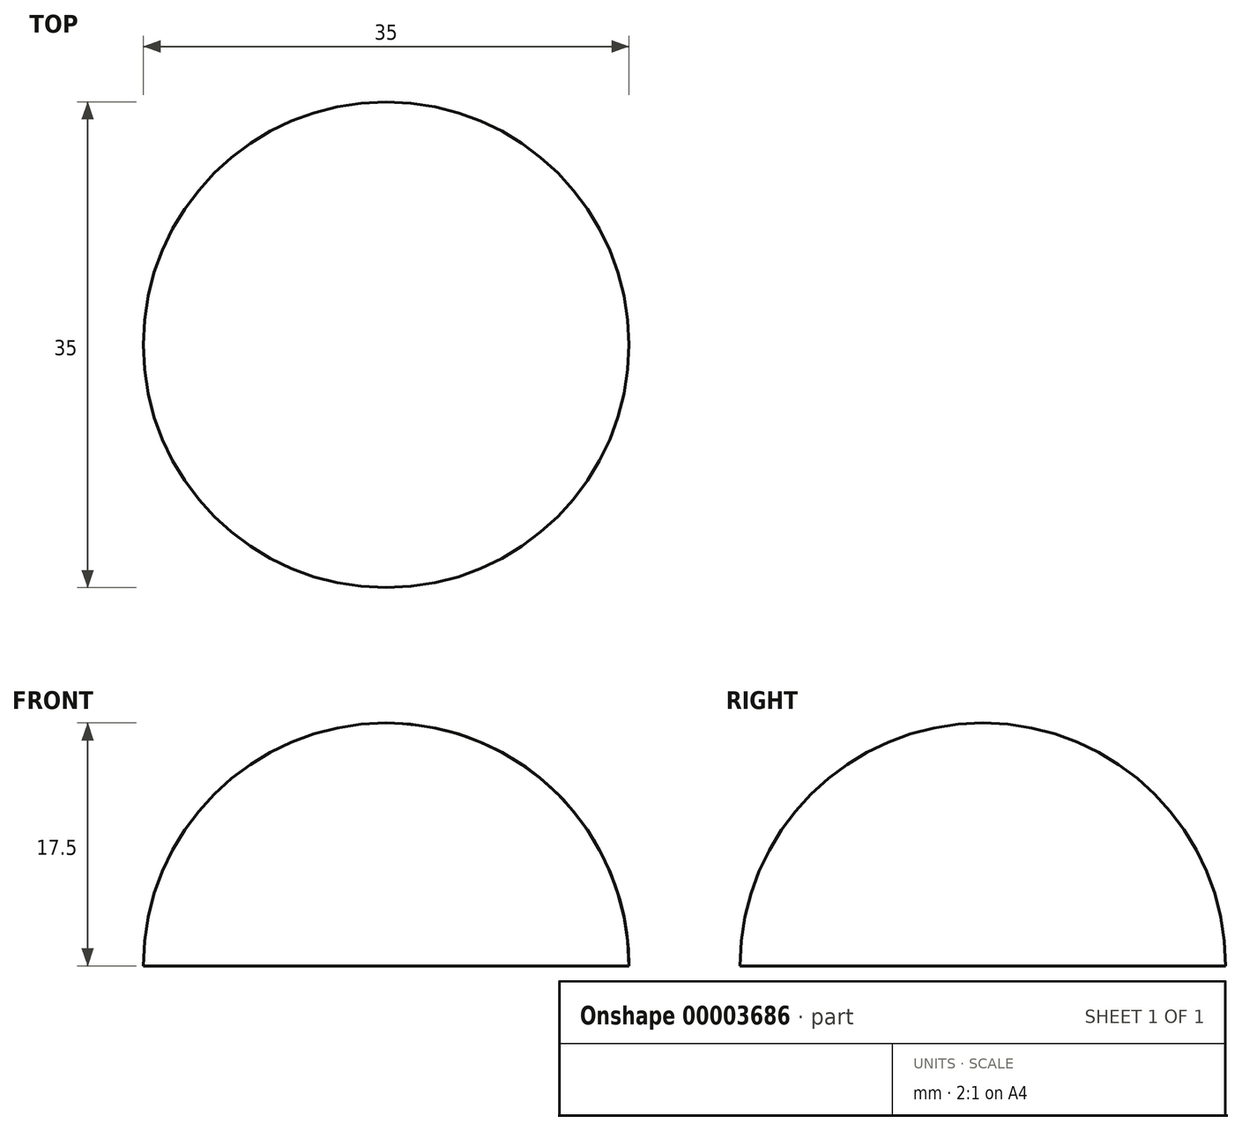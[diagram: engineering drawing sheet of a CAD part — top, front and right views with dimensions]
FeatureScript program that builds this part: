
annotation { "Feature Type Name" : "Feature", "Feature Type Description" : "" }
export const myFeature = defineFeature(function(context is Context, id is Id, definition is map)
    precondition{}
    {
        {
            var Q0;
            Q0=qCreatedBy(makeId("Front.planeOp"),FACE);
            var sketch = newSketch(context, id + "F0", { "sketchPlane" : qUnion([Q0])});
            skLineSegment(sketch, "E0", {"start": v(0, 0) * mm, "end": v(0, 17.5) * mm});
            skArc(sketch, "E1", {"start": v(17.5, 0) * mm, "mid": v(12.37, 12.37) * mm, "end": v(0, 17.5) * mm});
            skLineSegment(sketch, "E2", {"start": v(0, 0) * mm, "end": v(17.5, 0) * mm});
            skSolve(sketch);
        }
        {
            var Q0;
            Q0 = qSketchRegion(id + "F0", true);
            var Q1;
            Q1=sQuery(id+"F0.wireOp",EDGE,"E0");
            revolve(context, id + "F1", {"entities" : qUnion([Q0]), "axis" : qUnion([Q1]), "revolveType" : RevolveType.FULL});
        }
    });
